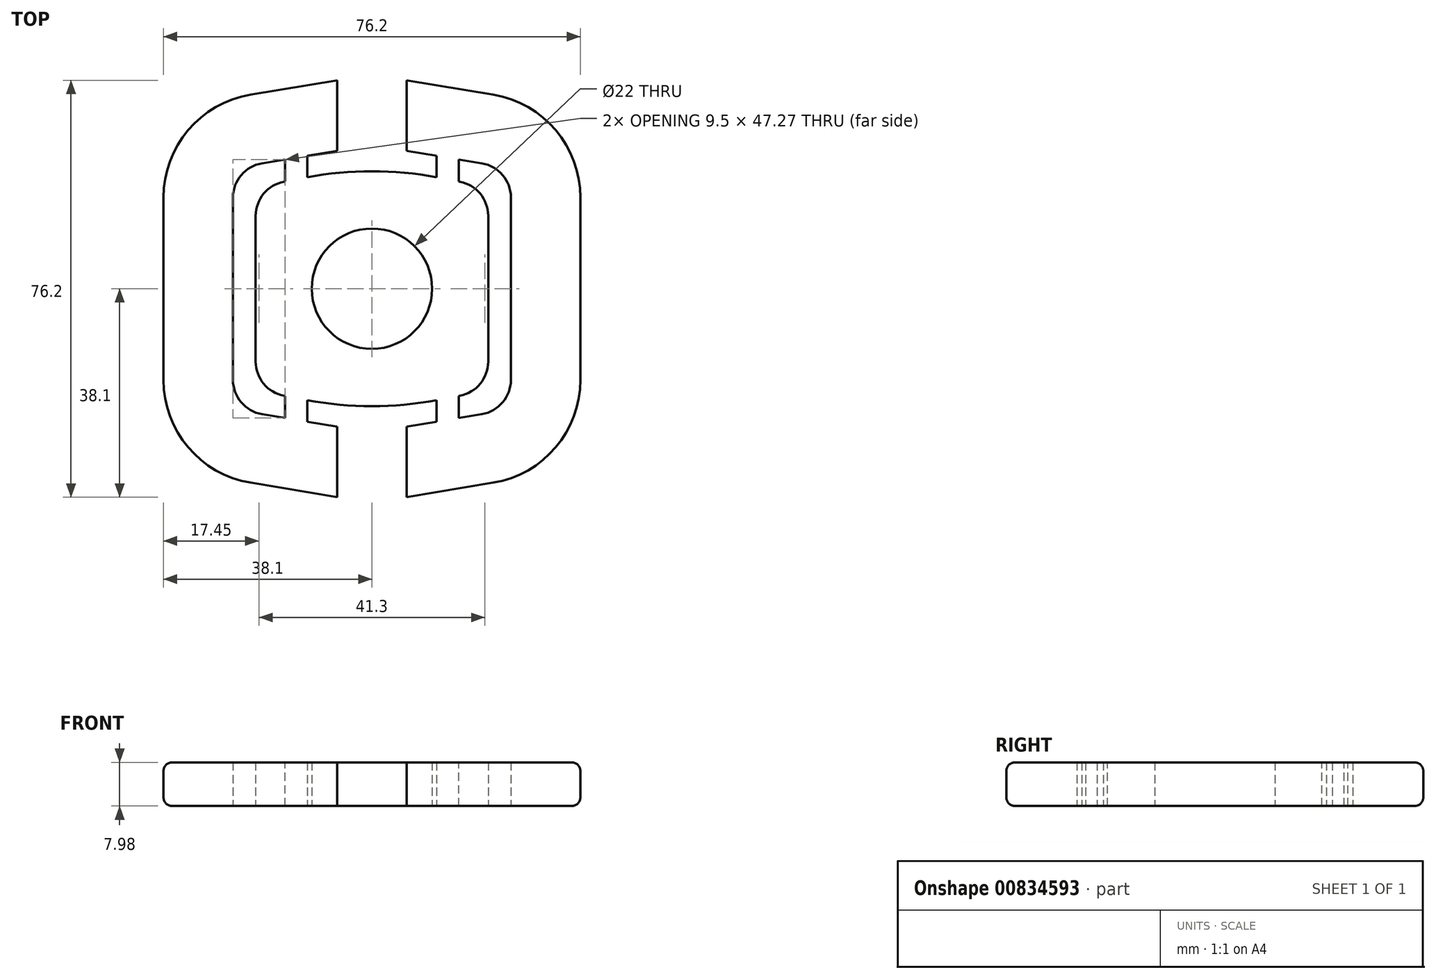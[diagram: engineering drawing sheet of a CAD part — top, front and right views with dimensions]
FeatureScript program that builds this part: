
annotation { "Feature Type Name" : "Feature", "Feature Type Description" : "" }
export const myFeature = defineFeature(function(context is Context, id is Id, definition is map)
    precondition{}
    {
        {
            var Q0;
            Q0=qCreatedBy(makeId("Top.planeOp"),FACE);
            var sketch = newSketch(context, id + "F0", { "sketchPlane" : qUnion([Q0])});
            skCircle(sketch, "E0", {"center": v(0, 0) * mm, "radius": 11 * mm});
            skLineSegment(sketch, "E1", {"start": v(0, 0) * mm, "end": v(0, 54.19) * mm, "construction": true});
            skLineSegment(sketch, "E2", {"start": v(-11.95, 20.35) * mm, "end": v(-16.09, 19.56) * mm});
            skLineSegment(sketch, "E3", {"start": v(-21.24, 13.32) * mm, "end": v(-21.24, 0) * mm});
            skPoint(sketch, "E4.visualSharp", {"position": v(-21.24, 18.57) * mm});
            skArc(sketch, "E4.filletArc", {"start": v(-16.09, 19.56) * mm, "mid": v(-19.79, 17.37) * mm, "end": v(-21.24, 13.32) * mm});
            skLineSegment(sketch, "E5", {"start": v(0, 0) * mm, "end": v(61.7, 0) * mm, "construction": true});
            skArc(sketch, "E6.MirrorCS", {"start": v(16.09, 19.56) * mm, "mid": v(19.79, 17.37) * mm, "end": v(21.24, 13.32) * mm});
            skLineSegment(sketch, "E7.MirrorCS", {"start": v(11.95, 20.35) * mm, "end": v(16.09, 19.56) * mm});
            skLineSegment(sketch, "E8.MirrorCS", {"start": v(21.24, 13.32) * mm, "end": v(21.24, 0) * mm});
            skPoint(sketch, "E9.MirrorP", {"position": v(21.24, 18.57) * mm});
            skArc(sketch, "E10.MirrorCS", {"start": v(16.09, -19.56) * mm, "mid": v(19.79, -17.37) * mm, "end": v(21.24, -13.32) * mm});
            skArc(sketch, "E11.MirrorCS", {"start": v(-16.09, -19.56) * mm, "mid": v(-19.79, -17.37) * mm, "end": v(-21.24, -13.32) * mm});
            skLineSegment(sketch, "E12.MirrorCS", {"start": v(11.95, -20.35) * mm, "end": v(16.09, -19.56) * mm});
            skLineSegment(sketch, "E13.MirrorCS", {"start": v(21.24, -13.32) * mm, "end": v(21.24, 0) * mm});
            skLineSegment(sketch, "E14.MirrorCS", {"start": v(-21.24, -13.32) * mm, "end": v(-21.24, 0) * mm});
            skPoint(sketch, "E15.MirrorP", {"position": v(-21.24, -18.57) * mm});
            skLineSegment(sketch, "E16.MirrorCS", {"start": v(-11.95, -20.35) * mm, "end": v(-16.09, -19.56) * mm});
            skPoint(sketch, "E17.MirrorP", {"position": v(21.24, -18.57) * mm});
            skPoint(sketch, "E18.visualSharp", {"position": v(0, 22.64) * mm});
            skArc(sketch, "E18.filletArc", {"start": v(11.95, 20.35) * mm, "mid": v(0, 21.49) * mm, "end": v(-11.95, 20.35) * mm});
            skPoint(sketch, "E19.visualSharp", {"position": v(0, -22.64) * mm});
            skArc(sketch, "E19.filletArc", {"start": v(-11.95, -20.35) * mm, "mid": v(0, -21.49) * mm, "end": v(11.95, -20.35) * mm});
            skSolve(sketch);
        }
        {
            var Q0;
            Q0 = qSketchRegion(id + "F0", true);
            extrude(context, id + "F1", {"entities" : qUnion([Q0]), "depth" : 7.98 * mm, "offsetDistance" : 25.4 * mm});
        }
        {
            var Q0;
            Q0=qCreatedBy(makeId("Top.planeOp"),FACE);
            var sketch = newSketch(context, id + "F2", { "sketchPlane" : qUnion([Q0])});
            skLineSegment(sketch, "E20", {"start": v(0, 0) * mm, "end": v(0, -94.48) * mm, "construction": true});
            skLineSegment(sketch, "E21", {"start": v(-38.1, 16.67) * mm, "end": v(-38.1, -16.67) * mm});
            skLineSegment(sketch, "E22", {"start": v(-6.35, 38.1) * mm, "end": v(-22.18, 35.46) * mm});
            skLineSegment(sketch, "E23", {"start": v(0, 0) * mm, "end": v(99.26, 0) * mm, "construction": true});
            skArc(sketch, "E24", {"start": v(-38.1, 16.67) * mm, "mid": v(-33.59, 28.98) * mm, "end": v(-22.18, 35.46) * mm});
            skLineSegment(sketch, "E25.0", {"start": v(-6.35, 25.22) * mm, "end": v(-20.1, 22.93) * mm});
            skArc(sketch, "E25.1", {"start": v(-25.4, 16.67) * mm, "mid": v(-23.9, 20.78) * mm, "end": v(-20.1, 22.93) * mm});
            skLineSegment(sketch, "E26", {"start": v(-6.35, 38.1) * mm, "end": v(-6.35, 25.22) * mm});
            skArc(sketch, "E27.MirrorCS", {"start": v(-25.4, -16.67) * mm, "mid": v(-23.9, -20.78) * mm, "end": v(-20.1, -22.93) * mm});
            skLineSegment(sketch, "E28.MirrorCS", {"start": v(-6.35, -25.22) * mm, "end": v(-20.1, -22.93) * mm});
            skLineSegment(sketch, "E29.MirrorCS", {"start": v(-6.35, -38.1) * mm, "end": v(-6.35, -25.22) * mm});
            skLineSegment(sketch, "E30.MirrorCS", {"start": v(-6.35, -38.1) * mm, "end": v(-22.18, -35.46) * mm});
            skArc(sketch, "E31.MirrorCS", {"start": v(-38.1, -16.67) * mm, "mid": v(-33.59, -28.98) * mm, "end": v(-22.18, -35.46) * mm});
            skLineSegment(sketch, "E32", {"start": v(-25.4, 16.67) * mm, "end": v(-25.4, -16.67) * mm});
            skArc(sketch, "E33.MirrorCS", {"start": v(38.1, 16.67) * mm, "mid": v(33.59, 28.98) * mm, "end": v(22.18, 35.46) * mm});
            skLineSegment(sketch, "E34.MirrorCS", {"start": v(38.1, 16.67) * mm, "end": v(38.1, -16.67) * mm});
            skArc(sketch, "E35.MirrorCS", {"start": v(25.4, 16.67) * mm, "mid": v(23.9, 20.78) * mm, "end": v(20.1, 22.93) * mm});
            skArc(sketch, "E36.MirrorCS", {"start": v(38.1, -16.67) * mm, "mid": v(33.59, -28.98) * mm, "end": v(22.18, -35.46) * mm});
            skLineSegment(sketch, "E37.MirrorCS", {"start": v(25.4, 16.67) * mm, "end": v(25.4, -16.67) * mm});
            skLineSegment(sketch, "E38.MirrorCS", {"start": v(6.35, 38.1) * mm, "end": v(6.35, 25.22) * mm});
            skLineSegment(sketch, "E39.MirrorCS", {"start": v(6.35, 25.22) * mm, "end": v(20.1, 22.93) * mm});
            skLineSegment(sketch, "E40.MirrorCS", {"start": v(6.35, 38.1) * mm, "end": v(22.18, 35.46) * mm});
            skLineSegment(sketch, "E41.MirrorCS", {"start": v(6.35, -38.1) * mm, "end": v(22.18, -35.46) * mm});
            skArc(sketch, "E42.MirrorCS", {"start": v(25.4, -16.67) * mm, "mid": v(23.9, -20.78) * mm, "end": v(20.1, -22.93) * mm});
            skLineSegment(sketch, "E43.MirrorCS", {"start": v(6.35, -25.22) * mm, "end": v(20.1, -22.93) * mm});
            skLineSegment(sketch, "E44.MirrorCS", {"start": v(6.35, -38.1) * mm, "end": v(6.35, -25.22) * mm});
            skSolve(sketch);
        }
        {
            var Q0;
            Q0 = qSketchRegion(id + "F2", true);
            extrude(context, id + "F3", {"entities" : qUnion([Q0]), "depth" : 7.98 * mm, "offsetDistance" : 25.4 * mm});
        }
        {
            var Q0;
            Q0=qCreatedBy(makeId("Top.planeOp"),FACE);
            var sketch = newSketch(context, id + "F4", { "sketchPlane" : qUnion([Q0])});
            skLineSegment(sketch, "E45.bottom", {"start": v(-15.9, 26.97) * mm, "end": v(-11.83, 26.97) * mm});
            skLineSegment(sketch, "E45.top", {"start": v(-15.9, 16.03) * mm, "end": v(-11.83, 16.03) * mm});
            skLineSegment(sketch, "E45.left", {"start": v(-15.9, 26.97) * mm, "end": v(-15.9, 16.03) * mm});
            skLineSegment(sketch, "E45.right", {"start": v(-11.83, 26.97) * mm, "end": v(-11.83, 16.03) * mm});
            skLineSegment(sketch, "E46", {"start": v(0, 0) * mm, "end": v(0, 52.66) * mm, "construction": true});
            skLineSegment(sketch, "E47", {"start": v(0, 0) * mm, "end": v(67.54, 0) * mm, "construction": true});
            skLineSegment(sketch, "E48.MirrorCS", {"start": v(15.9, 16.03) * mm, "end": v(11.83, 16.03) * mm});
            skLineSegment(sketch, "E49.MirrorCS", {"start": v(15.9, 26.97) * mm, "end": v(15.9, 16.03) * mm});
            skLineSegment(sketch, "E50.MirrorCS", {"start": v(11.83, 26.97) * mm, "end": v(11.83, 16.03) * mm});
            skLineSegment(sketch, "E51.MirrorCS", {"start": v(15.9, 26.97) * mm, "end": v(11.83, 26.97) * mm});
            skLineSegment(sketch, "E52.MirrorCS", {"start": v(11.83, -26.97) * mm, "end": v(11.83, -16.03) * mm});
            skLineSegment(sketch, "E53.MirrorCS", {"start": v(15.9, -26.97) * mm, "end": v(11.83, -26.97) * mm});
            skLineSegment(sketch, "E54.MirrorCS", {"start": v(15.9, -26.97) * mm, "end": v(15.9, -16.03) * mm});
            skLineSegment(sketch, "E55.MirrorCS", {"start": v(15.9, -16.03) * mm, "end": v(11.83, -16.03) * mm});
            skLineSegment(sketch, "E56.MirrorCS", {"start": v(-15.9, -16.03) * mm, "end": v(-11.83, -16.03) * mm});
            skLineSegment(sketch, "E57.MirrorCS", {"start": v(-11.83, -26.97) * mm, "end": v(-11.83, -16.03) * mm});
            skLineSegment(sketch, "E58.MirrorCS", {"start": v(-15.9, -26.97) * mm, "end": v(-15.9, -16.03) * mm});
            skLineSegment(sketch, "E59.MirrorCS", {"start": v(-15.9, -26.97) * mm, "end": v(-11.83, -26.97) * mm});
            skSolve(sketch);
        }
        {
            var Q0;
            Q0 = qSketchRegion(id + "F4", true);
            extrude(context, id + "F5", {"entities" : qUnion([Q0]), "operationType" : NewBodyOperationType.ADD, "depth" : 7.98 * mm, "offsetDistance" : 25.4 * mm});
        }
        {
            var Q0;
            Q0=makeQuery(id+"F3.opExtrude","CAP_EDGE",EDGE,{"disambiguationData":[OSD([sQuery(id+"F2.wireOp",EDGE,"E30.MirrorCS")])],"isStart":false});
            var Q1;
            Q1=makeQuery(id+"F3.opExtrude","CAP_EDGE",EDGE,{"disambiguationData":[OSD([sQuery(id+"F2.wireOp",EDGE,"E41.MirrorCS")])],"isStart":false});
            var Q2;
            Q2=makeQuery(id+"F3.opExtrude","CAP_EDGE",EDGE,{"disambiguationData":[OSD([sQuery(id+"F2.wireOp",EDGE,"E41.MirrorCS")])],"isStart":true});
            var Q3;
            Q3=makeQuery(id+"F3.opExtrude","CAP_EDGE",EDGE,{"disambiguationData":[OSD([sQuery(id+"F2.wireOp",EDGE,"E30.MirrorCS")])],"isStart":true});
            fillet(context, id + "F6", {"entities" : qUnion([Q0, Q1, Q2, Q3]), "radius" : 1.59 * mm, "tangentPropagation" : true, "allowEdgeOverflow" : false});
        }
    });
